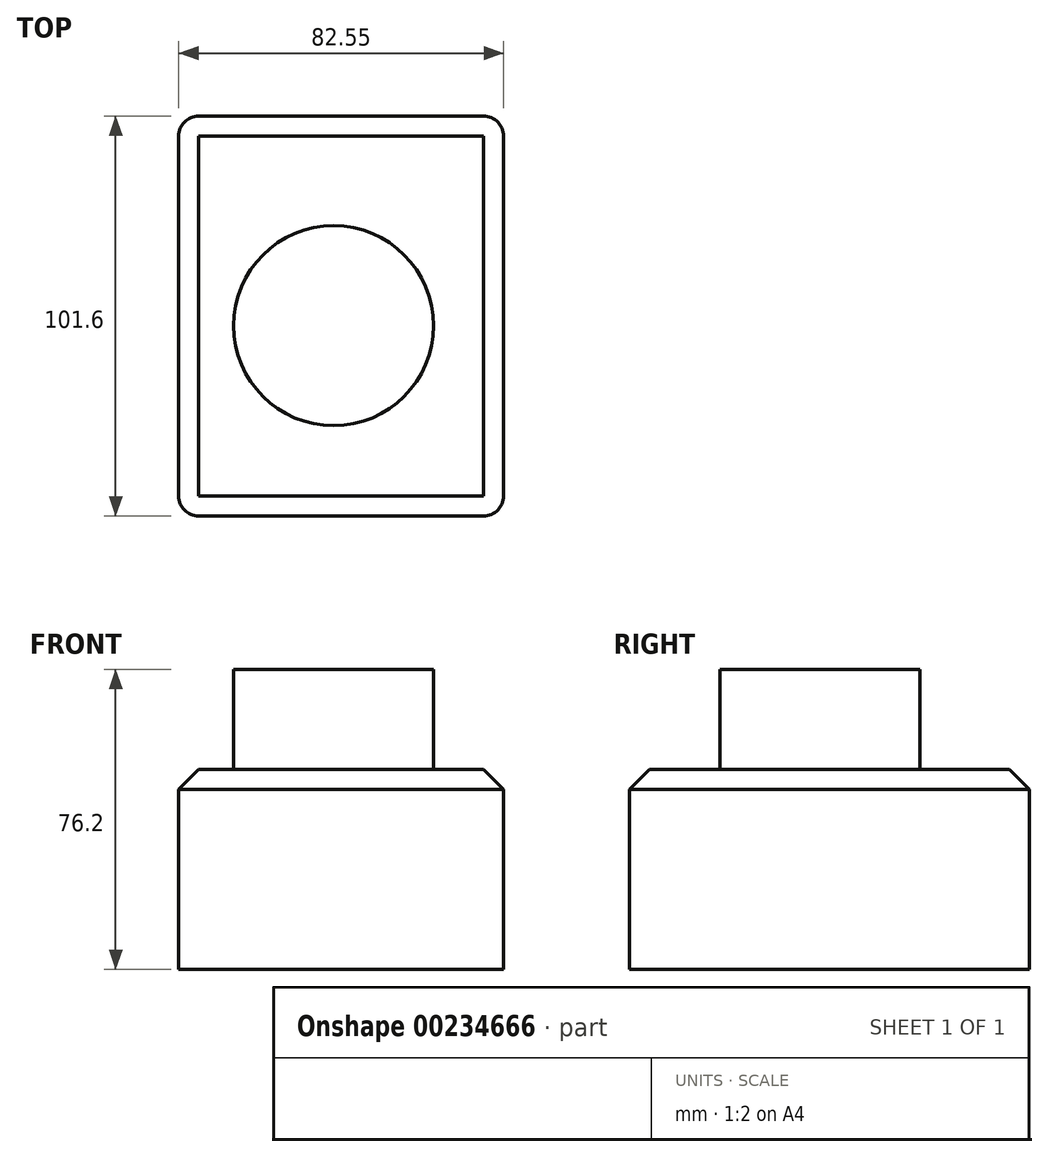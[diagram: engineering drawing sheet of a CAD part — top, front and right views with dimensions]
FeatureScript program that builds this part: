
annotation { "Feature Type Name" : "Feature", "Feature Type Description" : "" }
export const myFeature = defineFeature(function(context is Context, id is Id, definition is map)
    precondition{}
    {
        {
            var Q0;
            Q0=qCreatedBy(makeId("Front.planeOp"),FACE);
            var sketch = newSketch(context, id + "F0", { "sketchPlane" : qUnion([Q0])});
            skLineSegment(sketch, "E0.bottom", {"start": v(0, 0) * mm, "end": v(82.55, 0) * mm});
            skLineSegment(sketch, "E0.top", {"start": v(0, 50.8) * mm, "end": v(82.55, 50.8) * mm});
            skLineSegment(sketch, "E0.left", {"start": v(0, 0) * mm, "end": v(0, 50.8) * mm});
            skLineSegment(sketch, "E0.right", {"start": v(82.55, 0) * mm, "end": v(82.55, 50.8) * mm});
            skSolve(sketch);
        }
        {
            var Q0;
            Q0=makeQuery(id+"F0.imprint","IMPRINT",FACE,{"disambiguationData":[TD([[makeQuery(id+"F0.imprint","IMPRINT",EDGE,{"derivedFrom":sQuery(id+"F0.wireOp",EDGE,"E0.bottom")}),1.0]])]});
            extrude(context, id + "F1", {"entities" : qUnion([Q0]), "depth" : 101.6 * mm});
        }
        {
            var Q0;
            Q0=makeQuery(id+"F1.opExtrude","CAP_EDGE",EDGE,{"disambiguationData":[OSD([sQuery(id+"F0.wireOp",EDGE,"E0.left")])],"isStart":false});
            var Q1;
            Q1=makeQuery(id+"F1.opExtrude","CAP_EDGE",EDGE,{"disambiguationData":[OSD([sQuery(id+"F0.wireOp",EDGE,"E0.right")])],"isStart":false});
            var Q2;
            Q2=makeQuery(id+"F1.opExtrude","CAP_EDGE",EDGE,{"disambiguationData":[OSD([sQuery(id+"F0.wireOp",EDGE,"E0.right")])],"isStart":true});
            var Q3;
            Q3=makeQuery(id+"F1.opExtrude","CAP_EDGE",EDGE,{"disambiguationData":[OSD([sQuery(id+"F0.wireOp",EDGE,"E0.left")])],"isStart":true});
            fillet(context, id + "F2", {"entities" : qUnion([Q0, Q1, Q2, Q3]), "radius" : 5.08 * mm, "tangentPropagation" : true, "allowEdgeOverflow" : false});
        }
        {
            var Q0;
            Q0=makeQuery(id+"F1.opExtrude","CAP_EDGE",EDGE,{"disambiguationData":[OSD([sQuery(id+"F0.wireOp",EDGE,"E0.top")])],"isStart":false});
            chamfer(context, id + "F3", {"entities" : qUnion([Q0]), "width" : 5.08 * mm, "tangentPropagation" : true});
        }
        {
            var Q0;
            Q0=makeQuery(id+"F1.opExtrude","SWEPT_FACE",FACE,{"disambiguationData":[OSD([sQuery(id+"F0.wireOp",EDGE,"E0.top")])]});
            var sketch = newSketch(context, id + "F4", { "sketchPlane" : qUnion([Q0])});
            skCircle(sketch, "E1", {"center": v(39.34, -53.24) * mm, "radius": 25.4 * mm});
            skSolve(sketch);
        }
        {
            var Q0;
            Q0 = qSketchRegion(id + "F4", true);
            extrude(context, id + "F5", {"entities" : qUnion([Q0]), "operationType" : NewBodyOperationType.ADD, "depth" : 25.4 * mm});
        }
    });
